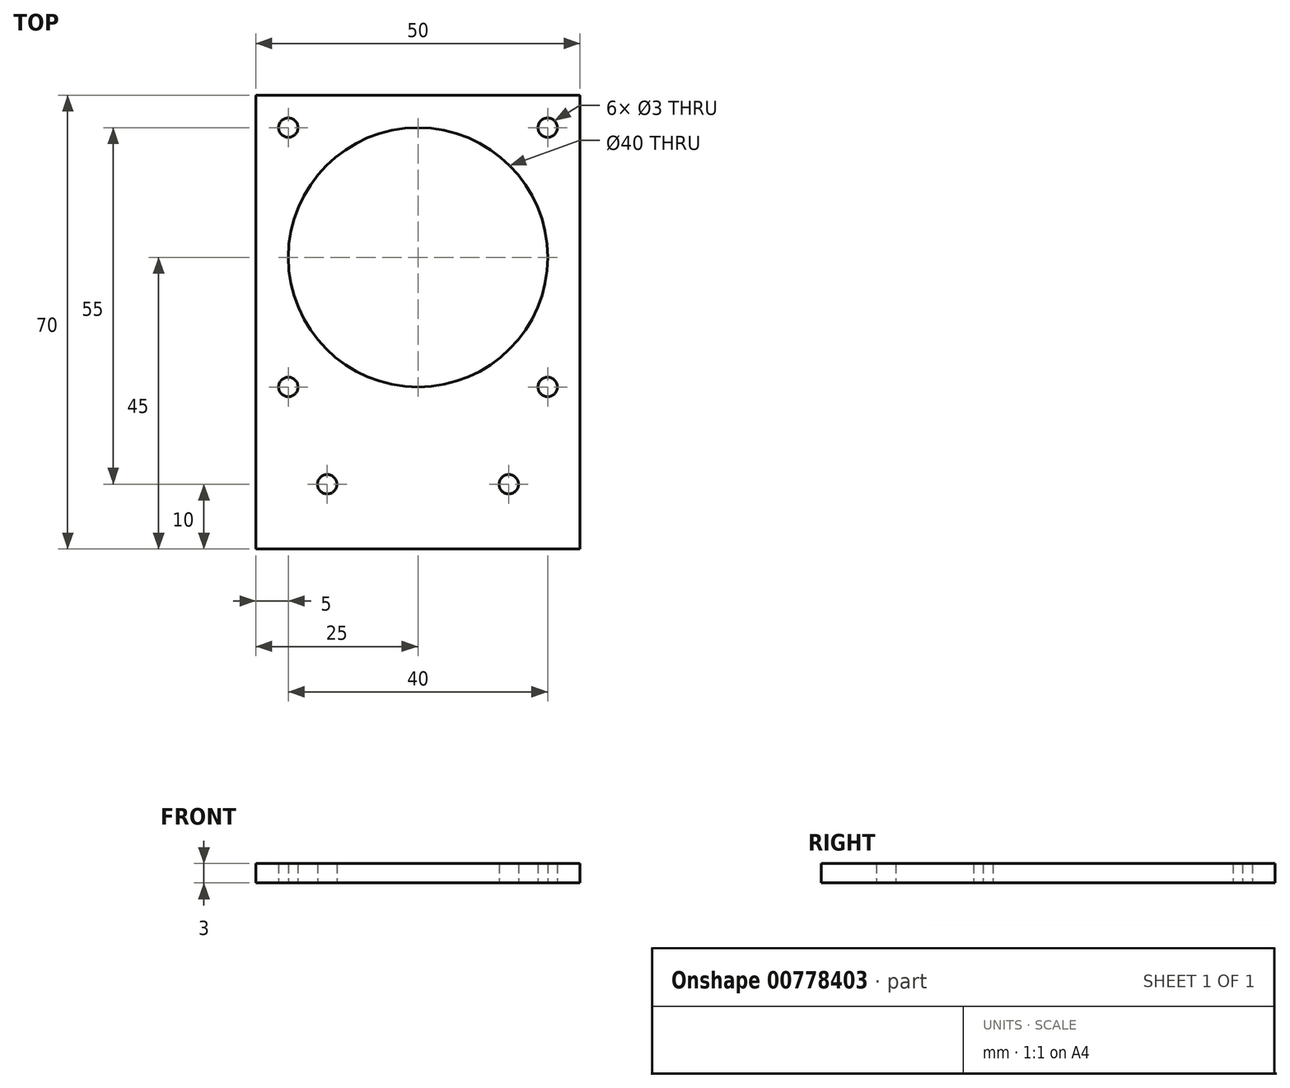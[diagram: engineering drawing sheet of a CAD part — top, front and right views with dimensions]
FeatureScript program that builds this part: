
annotation { "Feature Type Name" : "Feature", "Feature Type Description" : "" }
export const myFeature = defineFeature(function(context is Context, id is Id, definition is map)
    precondition{}
    {
        {
            var Q0;
            Q0=qCreatedBy(makeId("Top.planeOp"),FACE);
            var sketch = newSketch(context, id + "F0", { "sketchPlane" : qUnion([Q0])});
            skLineSegment(sketch, "E0.bottom", {"start": v(25, -25) * mm, "end": v(-25, -25) * mm});
            skLineSegment(sketch, "E0.top", {"start": v(25, 25) * mm, "end": v(-25, 25) * mm});
            skLineSegment(sketch, "E0.left", {"start": v(25, -25) * mm, "end": v(25, 25) * mm});
            skLineSegment(sketch, "E0.right", {"start": v(-25, -25) * mm, "end": v(-25, 25) * mm});
            skPoint(sketch, "E0.middle", {"position": v(0, 0) * mm});
            skLineSegment(sketch, "E1.bottom", {"start": v(20, -20) * mm, "end": v(-20, -20) * mm});
            skLineSegment(sketch, "E1.top", {"start": v(20, 20) * mm, "end": v(-20, 20) * mm});
            skLineSegment(sketch, "E1.left", {"start": v(20, -20) * mm, "end": v(20, 20) * mm});
            skLineSegment(sketch, "E1.right", {"start": v(-20, -20) * mm, "end": v(-20, 20) * mm});
            skSolve(sketch);
        }
        {
            var Q0;
            Q0=makeQuery(id+"F0.imprint","IMPRINT",FACE,{"disambiguationData":[TD([[makeQuery(id+"F0.imprint","IMPRINT",EDGE,{"derivedFrom":sQuery(id+"F0.wireOp",EDGE,"E1.bottom")}),-1.0]])]});
            var Q1;
            Q1=makeQuery(id+"F0.imprint","IMPRINT",FACE,{"disambiguationData":[TD([[makeQuery(id+"F0.imprint","IMPRINT",EDGE,{"derivedFrom":sQuery(id+"F0.wireOp",EDGE,"E0.bottom")}),-1.0]])]});
            extrude(context, id + "F1", {"entities" : qUnion([Q0, Q1]), "depth" : 3 * mm, "offsetDistance" : 25 * mm});
        }
        {
            var Q0;
            Q0=sQuery(id+"F0.wireOp",VERTEX,"E1.bottom.end");
            var Q1;
            Q1=sQuery(id+"F0.wireOp",VERTEX,"E1.bottom.start");
            var Q2;
            Q2=sQuery(id+"F0.wireOp",VERTEX,"E1.top.start");
            var Q3;
            Q3=sQuery(id+"F0.wireOp",VERTEX,"E1.top.end");
            var Q4;
            Q4=makeQuery(id+"F1.opExtrude","SWEPT_BODY",BODY,{"disambiguationData":[OSD([sQuery(id+"F0.wireOp",EDGE,"E0.bottom"),sQuery(id+"F0.wireOp",EDGE,"E0.top"),sQuery(id+"F0.wireOp",EDGE,"E0.left"),sQuery(id+"F0.wireOp",EDGE,"E0.right")])]});
            hole(context, id + "F2", {"style" : HoleStyle.SIMPLE, "endStyle" : HoleEndStyle.THROUGH, "oppositeDirection" : true, "holeDiameter" : 3 * mm, "majorDiameter" : 5 * mm, "isTappedThrough" : true, "tappedDepth" : 12 * mm, "tapClearance" : 3, "locations" : qUnion([Q0, Q1, Q2, Q3]), "scope" : qUnion([Q4])});
        }
        {
            var Q0;
            Q0=makeQuery(id+"F1.opExtrude","SWEPT_FACE",FACE,{"disambiguationData":[OSD([sQuery(id+"F0.wireOp",EDGE,"E0.bottom")])]});
            extrude(context, id + "F3", {"entities" : qUnion([Q0]), "operationType" : NewBodyOperationType.ADD, "depth" : 20 * mm, "offsetDistance" : 25 * mm});
        }
        {
            var Q0;
            {var subQ0=sQuery(id+"F0.wireOp",EDGE,"E0.bottom");Q0=makeQuery(id+"F3.boolean.opBoolean","MERGE",FACE,{"derivedFrom":[makeQuery(id+"F1.opExtrude","CAP_FACE",FACE,{"disambiguationData":[OSD([subQ0,sQuery(id+"F0.wireOp",EDGE,"E0.top"),sQuery(id+"F0.wireOp",EDGE,"E0.left"),sQuery(id+"F0.wireOp",EDGE,"E0.right")])],"isStart":true}),makeQuery(id+"F3.opExtrude","SWEPT_FACE",FACE,{"disambiguationData":[OSD([subQ0]),TDD([makeQuery(id+"F1.opExtrude","CAP_EDGE",EDGE,{"disambiguationData":[OSD([subQ0])],"isStart":true})])]})]});}
            var sketch = newSketch(context, id + "F4", { "sketchPlane" : qUnion([Q0])});
            skLineSegment(sketch, "E2", {"start": v(14, 35) * mm, "end": v(-14, 35) * mm});
            skSolve(sketch);
        }
        {
            var Q0;
            Q0=sQuery(id+"F4.wireOp",VERTEX,"E2.start");
            var Q1;
            Q1=sQuery(id+"F4.wireOp",VERTEX,"E2.end");
            var Q2;
            Q2=makeQuery(id+"F1.opExtrude","SWEPT_BODY",BODY,{"disambiguationData":[OSD([sQuery(id+"F0.wireOp",EDGE,"E0.bottom"),sQuery(id+"F0.wireOp",EDGE,"E0.top"),sQuery(id+"F0.wireOp",EDGE,"E0.left"),sQuery(id+"F0.wireOp",EDGE,"E0.right")])]});
            hole(context, id + "F5", {"style" : HoleStyle.SIMPLE, "endStyle" : HoleEndStyle.THROUGH, "holeDiameter" : 3 * mm, "majorDiameter" : 5 * mm, "isTappedThrough" : true, "tappedDepth" : 12 * mm, "tapClearance" : 3, "locations" : qUnion([Q0, Q1]), "scope" : qUnion([Q2])});
        }
        {
            var Q0;
            Q0=makeQuery(id+"F0.imprint","IMPRINT",FACE,{"disambiguationData":[TD([[makeQuery(id+"F0.imprint","IMPRINT",EDGE,{"derivedFrom":sQuery(id+"F0.wireOp",EDGE,"E1.bottom")}),-1.0]])]});
            var sketch = newSketch(context, id + "F6", { "sketchPlane" : qUnion([Q0])});
            skCircle(sketch, "E3", {"center": v(0, 0) * mm, "radius": 20 * mm});
            skSolve(sketch);
        }
        {
            var Q0;
            {var subQ0=sQuery(id+"F6.wireOp",EDGE,"E3");var subQ1=makeQuery(id+"F6.imprint","INTERSECT",VERTEX,{"derivedFrom":[makeQuery(id+"F0.imprint","IMPRINT",EDGE,{"derivedFrom":sQuery(id+"F0.wireOp",EDGE,"E1.top")}),subQ0]});Q0=makeQuery(id+"F6.imprint","IMPRINT",FACE,{"disambiguationData":[TD([[makeQuery(id+"F6.imprint","IMPRINT",EDGE,{"disambiguationData":[TD([[subQ1,1.0]])],"derivedFrom":subQ0}),1.0]])]});}
            var Q1;
            Q1=sQuery(id+"F6.wireOp",EDGE,"E3");
            extrude(context, id + "F7", {"entities" : qUnion([Q0]), "operationType" : NewBodyOperationType.REMOVE, "surfaceOperationType" : NewSurfaceOperationType.ADD, "surfaceEntities" : qUnion([Q1]), "depth" : 25 * mm, "offsetDistance" : 25 * mm});
        }
    });
